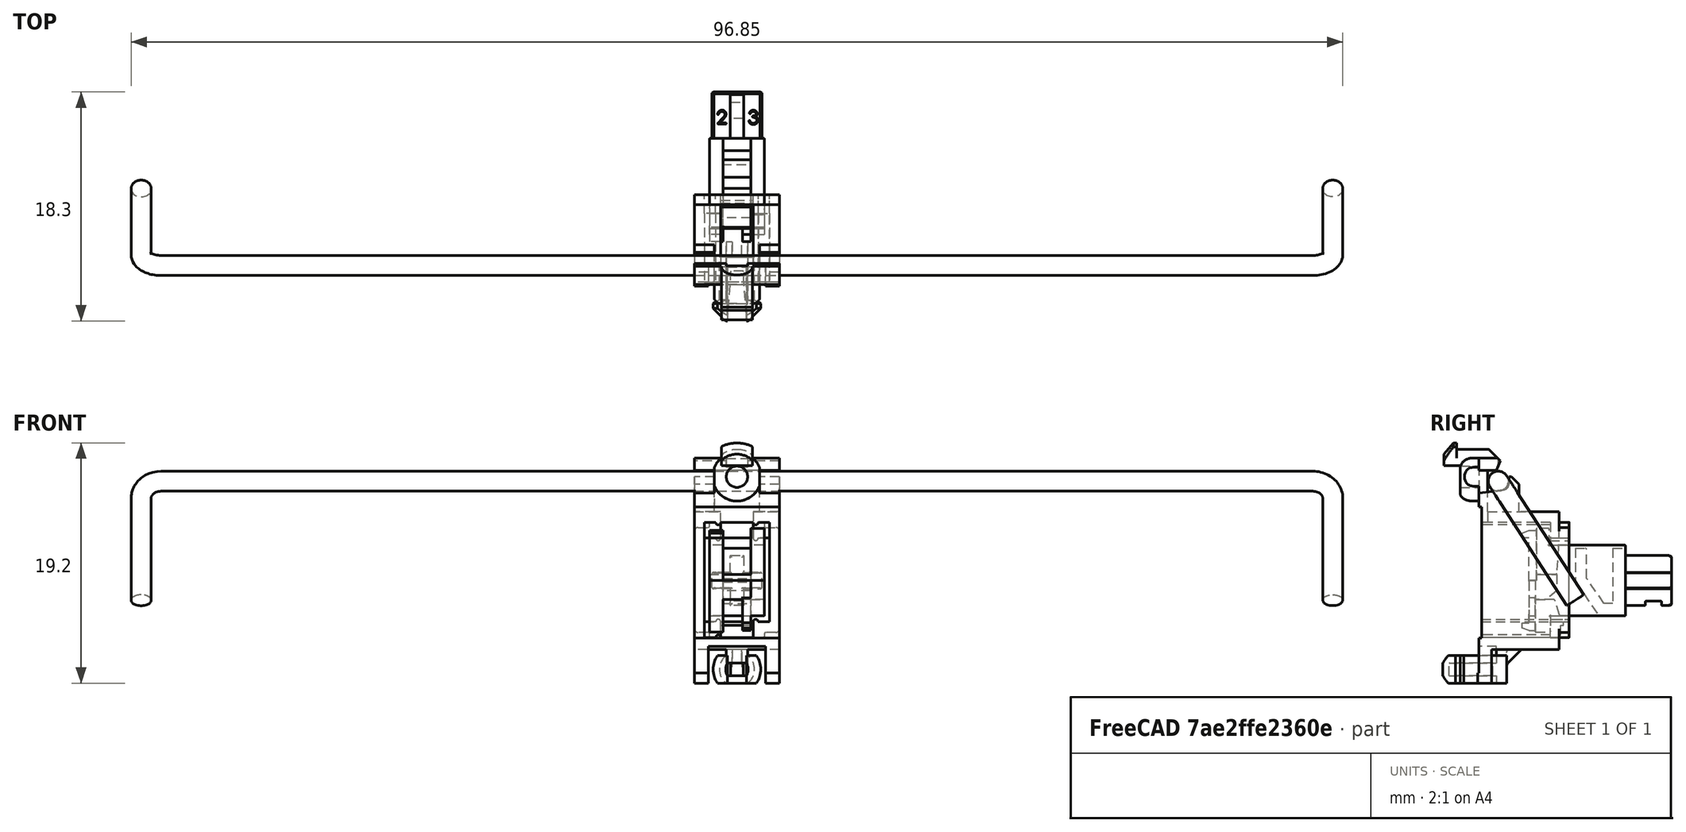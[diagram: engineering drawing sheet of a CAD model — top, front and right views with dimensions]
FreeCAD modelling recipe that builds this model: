
FCSTD DOCUMENT  (FreeCAD 0.18R16158 (Git))
Label: Stabilizer_Cherry_MX_6u
License: CreativeCommons Attribution-ShareAlike
LicenseURL: http://creativecommons.org/licenses/by-sa/4.0/
objects: Part::Feature×4, App::Part×3, PartDesign::Plane×2, Sketcher::SketchObject×2, PartDesign::AdditivePipe×1, PartDesign::Body×1
note: 11 computed .brp shape members not serialized (recipe doc carries the construction recipe); baked Part::Feature solids carry a one-line shape summary decoded from their .brp

FEATURE [Part::Feature] Part__Feature  label="Stabilizer_Base"
  shape: bbox 6.802 x 10.1 x 19.67 mm, 163 faces (baked)
FEATURE [Part::Feature] Part__Feature001  label="Stabilizer_Key"
  Placement = pos=(0,8.1,0) rot=(0,0,1;0rad)
  shape: bbox 4.6 x 11.96 x 8.302 mm, 299 faces (baked)
FEATURE [App::Part] Part  label="Stabilizer_End_1"
  Group = -> [Part__Feature001,Part__Feature]
  Origin = -> Origin001
  Placement = pos=(-47.63,0,0) rot=(0,0,1;0rad)
FEATURE [PartDesign::Plane] DatumPlane
  Length = 107.188
  MapMode = 13
  Placement = pos=(23.0333,0.289849,4.3056) rot=(1,0,0;2.14498rad)
  ResizeMode = 0
  Width = 38.0058
FEATURE [PartDesign::Plane] DatumPlane001
  Length = 38.0058
  MapMode = 11
  Placement = pos=(8e-15,4.09188,-1.57187) rot=(0.272451,-0.272451,0.92279;1.65106rad)
  ResizeMode = 0
  Width = 107.188
FEATURE [Sketcher::SketchObject] Sketch
  MapMode = 5
  Placement = pos=(8e-15,4.09188,-1.57187) rot=(0.272451,-0.272451,0.92279;1.65106rad)
  Support = -> [DatumPlane001]
  sketch-geometry (5):
    g0: Circle CenterX=0 CenterY=47.625 CenterZ=0 NormalX=0 NormalY=0 NormalZ=1 AngleXU=0 Radius=0.8
    g1: Circle [constr] CenterX=0 CenterY=-47.625 CenterZ=0 NormalX=0 NormalY=0 NormalZ=1 AngleXU=0 Radius=0.8
    g2: LineSegment [constr] StartX=0 StartY=47.625 StartZ=0 EndX=0 EndY=0 EndZ=0
    g3: LineSegment [constr] StartX=0 StartY=0 StartZ=0 EndX=0 EndY=-47.625 EndZ=0
    g4: GeomPoint X=0 Y=-47.625 Z=0
  constraints (11):
    c: Diameter(g0) = 1.6
    c: PointOnObject(g0,g-2)
    c: PointOnObject(g1,g-2)
    c: Coincident(g2,g0)
    c: Coincident(g2,g-1)
    c: Coincident(g3,g-1)
    c: Coincident(g3,g1)
    c: Equal(g3,g2)
    c: Distance(g2) = 47.625
    c: Equal(g1,g0)
    c: Coincident(g4,g1)
FEATURE [Sketcher::SketchObject] Sketch001
  ExternalGeometry = -> [Sketch]
  MapMode = 5
  Placement = pos=(23.0333,0.289849,4.3056) rot=(1,0,0;2.14498rad)
  Support = -> [DatumPlane]
  sketch-geometry (5):
    g0: LineSegment StartX=-69.8583 StartY=-6.99875 StartZ=0 EndX=-69.8583 EndY=2.73125 EndZ=0
    g1: LineSegment StartX=-69.0583 StartY=3.53125 StartZ=0 EndX=22.9917 EndY=3.53125 EndZ=0
    g2: LineSegment StartX=23.7917 StartY=2.73125 StartZ=0 EndX=23.7917 EndY=-6.99875 EndZ=0
    g3: ArcOfCircle CenterX=-69.0583 CenterY=2.73125 CenterZ=0 NormalX=0 NormalY=0 NormalZ=1 AngleXU=0 Radius=0.8 StartAngle=1.5708 EndAngle=3.14159
    g4: ArcOfCircle CenterX=22.9917 CenterY=2.73125 CenterZ=0 NormalX=0 NormalY=0 NormalZ=1 AngleXU=0 Radius=0.8 StartAngle=-6.39e-14 EndAngle=1.5708
FEATURE [PartDesign::AdditivePipe] AdditivePipe
  AuxilleryCurvelinear = true
  AuxillerySpineTangent = false
  Binormal = (0,0,0)
  Mode = 0
  Placement = pos=(8e-15,4.09188,-1.57187) rot=(0.272451,-0.272451,0.92279;1.65106rad)
  Profile = -> Sketch
  Spine = -> Sketch001
  SpineTangent = false
  Transformation = 0
  Transition = 0
FEATURE [PartDesign::Body] Body  label="Bar"
  Group = -> [DatumPlane,DatumPlane001,Sketch,Sketch001,AdditivePipe]
  Origin = -> Origin002
  Tip = -> AdditivePipe
FEATURE [Part::Feature] Part__Feature002  label="Stabilizer_Key_"
  Placement = pos=(0,8.1,0) rot=(0,0,1;0rad)
  shape: bbox 4.6 x 11.96 x 8.302 mm, 299 faces (baked)
FEATURE [Part::Feature] Part__Feature003  label="Stabilizer_Base_"
  shape: bbox 6.802 x 10.1 x 19.67 mm, 163 faces (baked)
FEATURE [App::Part] Part001  label="Stabilizer_End_2"
  Group = -> [Part__Feature002,Part__Feature003]
  Origin = -> Origin003
  Placement = pos=(47.625,0,0) rot=(0,0,1;0rad)
FEATURE [App::Part] Stabilizer___open  label="Stabilizer_Cherry_MX_6u"
  Group = -> [Body,Part001,Part]
  Origin = -> Origin
  Placement = pos=(0,8e-16,3.65) rot=(1,0,0;1.5708rad)
